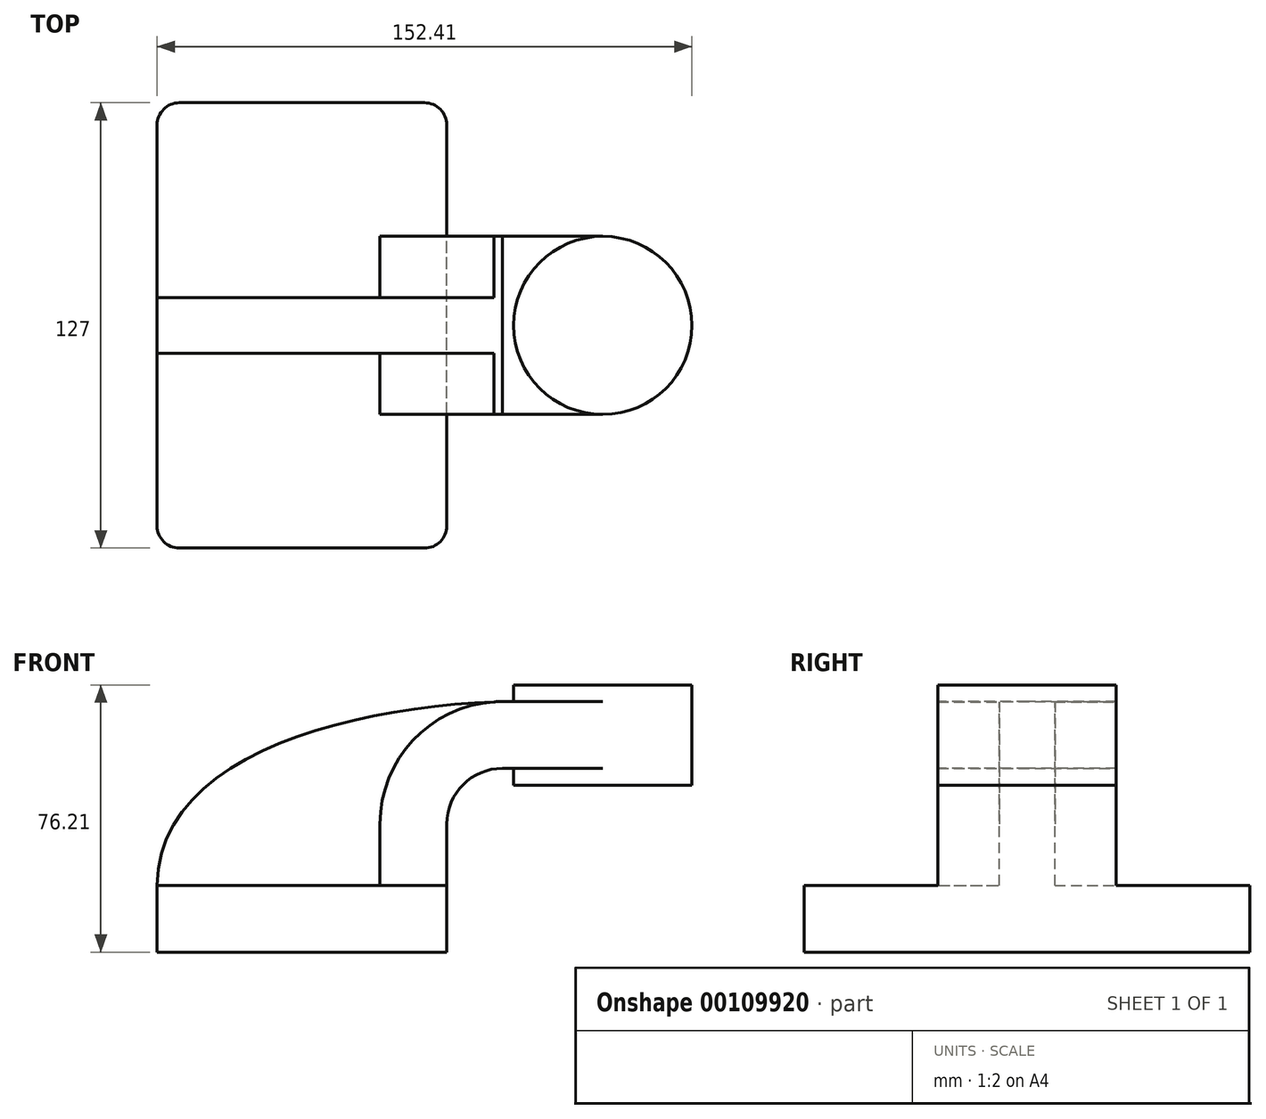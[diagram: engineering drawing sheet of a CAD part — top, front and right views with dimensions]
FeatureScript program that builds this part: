
annotation { "Feature Type Name" : "Feature", "Feature Type Description" : "" }
export const myFeature = defineFeature(function(context is Context, id is Id, definition is map)
    precondition{}
    {
        {
            var Q0;
            Q0=qCreatedBy(makeId("Front.planeOp"),FACE);
            var sketch = newSketch(context, id + "F0", { "sketchPlane" : qUnion([Q0])});
            skLineSegment(sketch, "E0.bottom", {"start": v(41.27, 9.53) * mm, "end": v(-41.28, 9.53) * mm});
            skLineSegment(sketch, "E0.top", {"start": v(41.28, -9.52) * mm, "end": v(-41.27, -9.52) * mm});
            skLineSegment(sketch, "E0.left", {"start": v(41.28, 9.53) * mm, "end": v(41.28, -9.52) * mm});
            skLineSegment(sketch, "E0.right", {"start": v(-41.28, 9.53) * mm, "end": v(-41.27, -9.52) * mm});
            skPoint(sketch, "E0.middle", {"position": v(0, 0) * mm});
            skLineSegment(sketch, "E1.bottom", {"start": v(60.33, 38.1) * mm, "end": v(111.12, 38.1) * mm});
            skLineSegment(sketch, "E1.top", {"start": v(60.33, 66.68) * mm, "end": v(111.12, 66.68) * mm});
            skLineSegment(sketch, "E1.left", {"start": v(60.33, 38.1) * mm, "end": v(60.33, 66.68) * mm});
            skLineSegment(sketch, "E1.right", {"start": v(111.13, 38.1) * mm, "end": v(111.12, 66.68) * mm});
            skPoint(sketch, "E1.middle", {"position": v(85.73, 52.39) * mm});
            skLineSegment(sketch, "E2", {"start": v(41.27, 9.53) * mm, "end": v(41.27, 27) * mm});
            skArc(sketch, "E3", {"start": v(41.27, 27) * mm, "mid": v(45.92, 38.23) * mm, "end": v(57.15, 42.88) * mm});
            skLineSegment(sketch, "E4", {"start": v(57.15, 42.88) * mm, "end": v(85.73, 42.88) * mm});
            skLineSegment(sketch, "E5.0", {"start": v(57.15, 61.93) * mm, "end": v(85.73, 61.93) * mm});
            skArc(sketch, "E5.1", {"start": v(22.23, 27) * mm, "mid": v(32.45, 51.7) * mm, "end": v(57.15, 61.93) * mm});
            skLineSegment(sketch, "E5.2", {"start": v(22.22, 9.53) * mm, "end": v(22.22, 27) * mm});
            skLineSegment(sketch, "E6", {"start": v(85.73, 38.1) * mm, "end": v(85.73, 66.68) * mm});
            skFitSpline(sketch, "E7", {"points": [v(-41.28, 9.52) * mm, v(57.15, 61.93) * mm], "startDerivative": vector(0.77, 112.6) * mm, "endDerivative": vector(127.64, 3.68) * mm});
            skSolve(sketch);
        }
        {
            var Q0;
            Q0=makeQuery(id+"F0.imprint","IMPRINT",FACE,{"disambiguationData":[TD([[makeQuery(id+"F0.imprint","IMPRINT",EDGE,{"derivedFrom":sQuery(id+"F0.wireOp",EDGE,"E0.top")}),-1.0]])]});
            extrude(context, id + "F1", {"entities" : qUnion([Q0]), "endBound" : BoundingType.SYMMETRIC, "depth" : 127 * mm});
        }
        {
            var Q0;
            {var subQ1=sQuery(id+"F0.wireOp",EDGE,"E2");Q0=makeQuery(id+"F0.imprint","IMPRINT",FACE,{"disambiguationData":[TD([[makeQuery(id+"F0.imprint","IMPRINT",EDGE,{"derivedFrom":subQ1}),1.0]])]});}
            var Q1;
            {var subQ0=sQuery(id+"F0.wireOp",EDGE,"E4");var subQ1=sQuery(id+"F0.wireOp",EDGE,"E1.left");var subQ2=makeQuery(id+"F0.imprint","INTERSECT",VERTEX,{"derivedFrom":[subQ1,subQ0]});Q1=makeQuery(id+"F0.imprint","IMPRINT",FACE,{"disambiguationData":[TD([[makeQuery(id+"F0.imprint","IMPRINT",EDGE,{"disambiguationData":[TD([[subQ2,-1.0]])],"derivedFrom":subQ1}),-1.0]])]});}
            extrude(context, id + "F2", {"entities" : qUnion([Q0, Q1]), "operationType" : NewBodyOperationType.ADD, "endBound" : BoundingType.SYMMETRIC, "depth" : 50.8 * mm});
        }
        {
            var Q0;
            {var subQ3=sQuery(id+"F0.wireOp",EDGE,"E5.2");Q0=makeQuery(id+"F0.imprint","IMPRINT",FACE,{"disambiguationData":[TD([[makeQuery(id+"F0.imprint","IMPRINT",EDGE,{"derivedFrom":subQ3}),1.0]])]});}
            extrude(context, id + "F3", {"entities" : qUnion([Q0]), "operationType" : NewBodyOperationType.ADD, "endBound" : BoundingType.SYMMETRIC, "depth" : 15.88 * mm});
        }
        {
            var Q0;
            {var subQ0=sQuery(id+"F0.wireOp",EDGE,"E1.right");Q0=makeQuery(id+"F0.imprint","IMPRINT",FACE,{"disambiguationData":[TD([[makeQuery(id+"F0.imprint","IMPRINT",EDGE,{"derivedFrom":subQ0}),1.0]])]});}
            var Q1;
            Q1=sQuery(id+"F0.wireOp",EDGE,"E6");
            revolve(context, id + "F4", {"operationType" : NewBodyOperationType.ADD, "entities" : qUnion([Q0]), "axis" : qUnion([Q1]), "revolveType" : RevolveType.FULL});
        }
        {
            var Q0;
            Q0=makeQuery(id+"F1.opExtrude","CAP_EDGE",EDGE,{"disambiguationData":[OSD([sQuery(id+"F0.wireOp",EDGE,"E0.right")])],"isStart":false});
            var Q1;
            Q1=makeQuery(id+"F1.opExtrude","CAP_EDGE",EDGE,{"disambiguationData":[OSD([sQuery(id+"F0.wireOp",EDGE,"E0.right")])],"isStart":true});
            var Q2;
            Q2=makeQuery(id+"F1.opExtrude","CAP_EDGE",EDGE,{"disambiguationData":[OSD([sQuery(id+"F0.wireOp",EDGE,"E0.left")])],"isStart":false});
            var Q3;
            Q3=makeQuery(id+"F1.opExtrude","CAP_EDGE",EDGE,{"disambiguationData":[OSD([sQuery(id+"F0.wireOp",EDGE,"E0.left")])],"isStart":true});
            fillet(context, id + "F5", {"entities" : qUnion([Q0, Q1, Q2, Q3]), "radius" : 6.35 * mm, "tangentPropagation" : true, "allowEdgeOverflow" : false});
        }
    });
